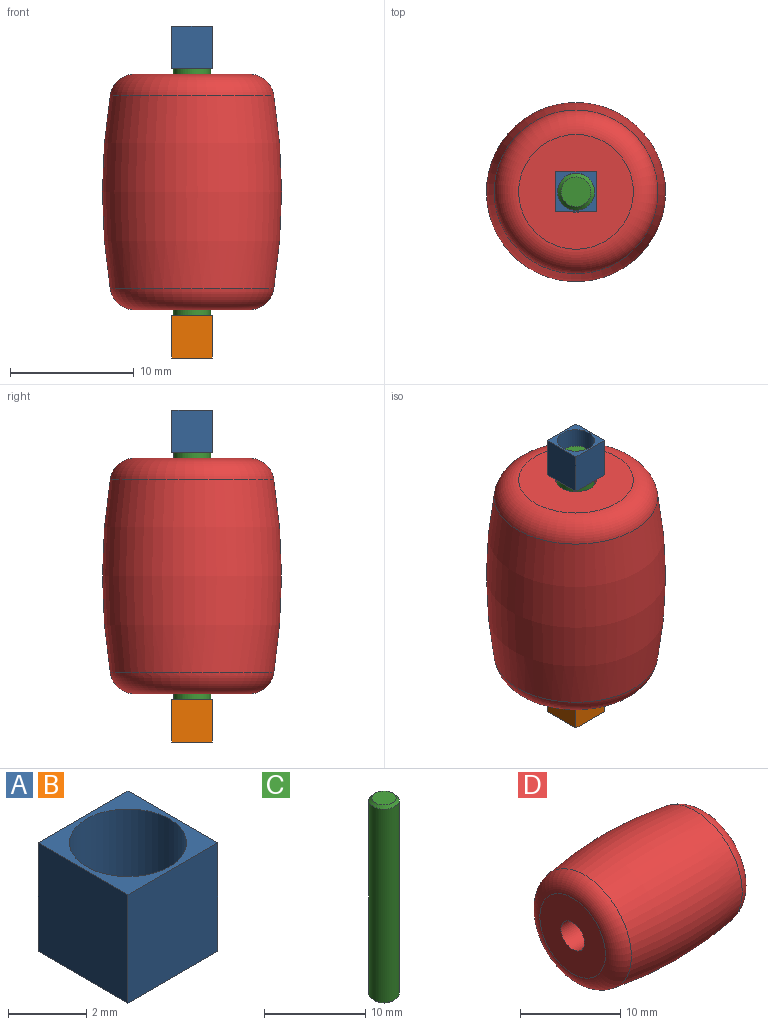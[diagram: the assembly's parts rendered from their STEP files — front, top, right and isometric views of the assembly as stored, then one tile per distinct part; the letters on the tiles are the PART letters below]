
ASSEMBLY  parts=4 mates=3
PART A: 7 faces, bbox 3.3x3.3x3.4 mm
  f0: plane 3.25x3.25mm, normal (0,0,-1), area 3.5mm2, adj f2,f3,f4,f5,f6
  f1: plane 3.25x3.25mm, normal (0,0,1), area 3.5mm2, adj f2,f3,f4,f5,f6
  f2: plane 3.4x3.25mm, normal (-1,0,0), area 11mm2, adj f0,f1,f3,f5
  f3: plane 3.4x3.25mm, normal (0,-1,0), area 11mm2, adj f0,f1,f2,f4
  f4: plane 3.4x3.25mm, normal (1,0,0), area 11.1mm2, adj f0,f1,f3,f5
  f5: plane 3.4x3.25mm, normal (0,1,0), area 11.1mm2, adj f0,f1,f2,f4
  f6: cylinder r=1.5mm len=3.4mm, axis (0,0,1), area 32mm2, adj f0,f1
PART B: same geometry as A
PART C: 5 faces, bbox 3x3x24 mm
  f0: plane 2.4x2.4mm, normal (0,0,-1), area 4.5mm2, adj f3
  f1: plane 2.4x2.4mm, normal (0,0,1), area 4.5mm2, adj f4
  f2: cylinder r=1.5mm len=23.4mm, axis (0,0,1), area 220.5mm2, adj f3,f4
  f3: cone r=1.5mm half-angle=45deg, axis (0,0,1), area 3.6mm2, adj f0,f2
  f4: cone r=1.5mm half-angle=45deg, axis (0,0,-1), area 3.6mm2, adj f1,f2
PART D: 6 faces, bbox 19x14.5x14.5 mm
  f0: revolved ~15.64x14.46mm, area 1385.6mm2, adj f4
  f1: plane 9.26x9.26mm, normal (-1,0,0), area 58.7mm2, adj f3,f5
  f2: plane 9.26x9.26mm, normal (1,0,0), area 58.7mm2, adj f3,f4
  f3: cylinder r=1.65mm len=19mm, axis (-1,0,0), area 197mm2, adj f1,f2
  f4: torus R=4.63mm, axis (-1,0,0), area 103.1mm2, adj f0,f2
  f5: torus R=4.63mm, axis (-1,0,0), area 103.1mm2, adj f1
PLACE A t=(0,0,10.5)mm
PLACE B rot(axis=(1,0,0),180deg) t=(0,0,-9.5)mm
PLACE C t=(0,0,0.5)mm
PLACE D rot(axis=(0,1,0),90deg) t=(0,0,0.5)mm
MATE fastened C.f2 <-> B.f6  axis (0,0,1) through (0,0,-11.2)mm
MATE fastened C.f2 <-> A.f6  axis (0,0,1) through (0,0,12.2)mm
MATE revolute D.f5 <-> C.f2  axis (0,0,1) through (0,0,0.5)mm
